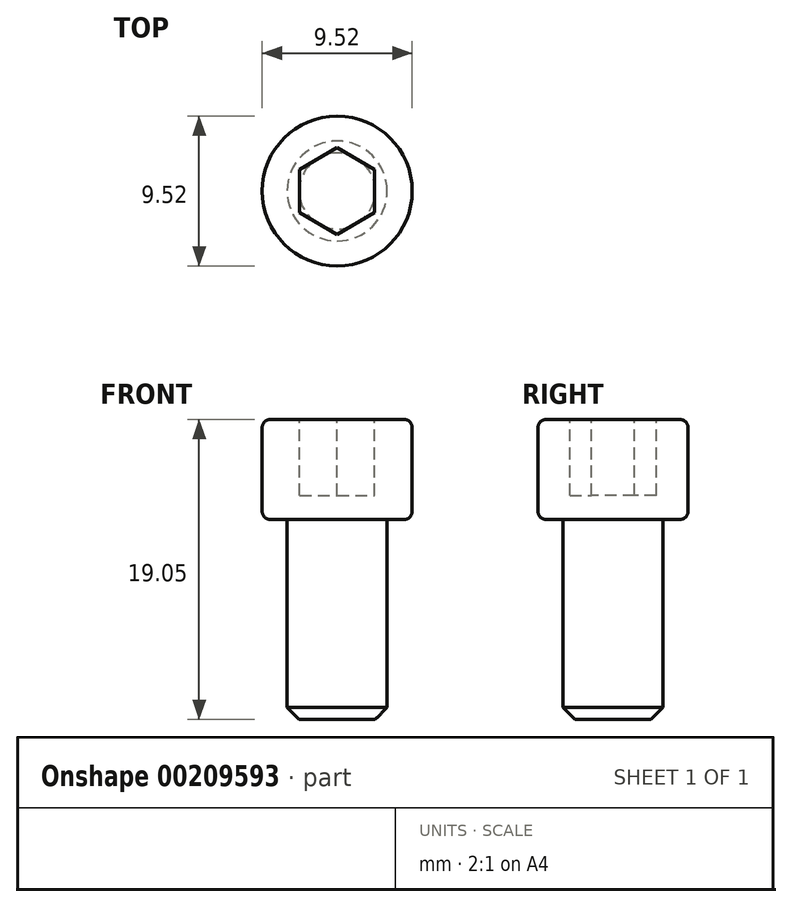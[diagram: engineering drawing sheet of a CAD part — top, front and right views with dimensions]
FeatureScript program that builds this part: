
annotation { "Feature Type Name" : "Feature", "Feature Type Description" : "" }
export const myFeature = defineFeature(function(context is Context, id is Id, definition is map)
    precondition{}
    {
        {
            var Q0;
            Q0=qCreatedBy(makeId("Top.planeOp"),FACE);
            var sketch = newSketch(context, id + "F0", { "sketchPlane" : qUnion([Q0])});
            skCircle(sketch, "E0", {"center": v(0, 0) * mm, "radius": 3.18 * mm});
            skSolve(sketch);
        }
        {
            var Q0;
            Q0=makeQuery(id+"F0.imprint","IMPRINT",FACE,{"disambiguationData":[TD([[makeQuery(id+"F0.imprint","IMPRINT",EDGE,{"derivedFrom":sQuery(id+"F0.wireOp",EDGE,"E0")}),1.0]])]});
            extrude(context, id + "F1", {"entities" : qUnion([Q0]), "oppositeDirection" : true, "depth" : 12.7 * mm});
        }
        {
            var Q0;
            Q0=qCreatedBy(makeId("Top.planeOp"),FACE);
            var sketch = newSketch(context, id + "F2", { "sketchPlane" : qUnion([Q0])});
            skCircle(sketch, "E1", {"center": v(0, 0) * mm, "radius": 4.76 * mm});
            skSolve(sketch);
        }
        {
            var Q0;
            Q0=makeQuery(id+"F2.imprint","IMPRINT",FACE,{"disambiguationData":[TD([[makeQuery(id+"F2.imprint","IMPRINT",EDGE,{"derivedFrom":sQuery(id+"F2.wireOp",EDGE,"E1")}),1.0]])]});
            extrude(context, id + "F3", {"entities" : qUnion([Q0]), "operationType" : NewBodyOperationType.ADD, "depth" : 6.35 * mm});
        }
        {
            var Q0;
            Q0=makeQuery(id+"F3.opExtrude","CAP_FACE",FACE,{"disambiguationData":[OSD([sQuery(id+"F2.wireOp",EDGE,"E1")])],"isStart":false});
            var sketch = newSketch(context, id + "F4", { "sketchPlane" : qUnion([Q0])});
            skCircle(sketch, "E2.cCircle", {"center": v(0, 0) * mm, "radius": 2.38 * mm, "construction": true});
            skLineSegment(sketch, "E2.0", {"start": v(2.38, 1.37) * mm, "end": v(2.38, -1.37) * mm});
            skLineSegment(sketch, "E2.1", {"start": v(2.38, -1.37) * mm, "end": v(0, -2.75) * mm});
            skLineSegment(sketch, "E2.2", {"start": v(0, -2.75) * mm, "end": v(-2.38, -1.37) * mm});
            skLineSegment(sketch, "E2.3", {"start": v(-2.38, -1.37) * mm, "end": v(-2.38, 1.37) * mm});
            skLineSegment(sketch, "E2.4", {"start": v(-2.38, 1.37) * mm, "end": v(0, 2.75) * mm});
            skLineSegment(sketch, "E2.5", {"start": v(0, 2.75) * mm, "end": v(2.38, 1.37) * mm});
            skPoint(sketch, "E2.0.midPoint", {"position": v(2.38, 0) * mm});
            skSolve(sketch);
        }
        {
            var Q0;
            Q0=makeQuery(id+"F4.imprint","IMPRINT",FACE,{"disambiguationData":[TD([[makeQuery(id+"F4.imprint","IMPRINT",EDGE,{"derivedFrom":sQuery(id+"F4.wireOp",EDGE,"E2.0")}),-1.0]])]});
            extrude(context, id + "F5", {"entities" : qUnion([Q0]), "operationType" : NewBodyOperationType.REMOVE, "oppositeDirection" : true, "depth" : 4.83 * mm});
        }
        {
            var Q0;
            Q0=makeQuery(id+"F1.opExtrude","CAP_EDGE",EDGE,{"disambiguationData":[OSD([sQuery(id+"F0.wireOp",EDGE,"E0")])],"isStart":false});
            chamfer(context, id + "F6", {"entities" : qUnion([Q0]), "chamferType" : ChamferType.OFFSET_ANGLE, "width" : 0.76 * mm, "oppositeDirection" : false, "angle" : 45 * degree, "tangentPropagation" : true});
        }
        {
            var Q0;
            Q0=qCreatedBy(makeId("Top.planeOp"),FACE);
            var Q1;
            Q1 = qBodyType(qCreatedBy(id + "F8" ,EDGE), BodyType.WIRE);
            cPlane(context, id + "F7", {"entities" : qUnion([Q0, Q1]), "cplaneType" : CPlaneType.OFFSET, "offset" : ((1 / 20) * 2) * mm, "oppositeDirection" : true, "width" : 152.4 * mm, "height" : 152.4 * mm});
        }
        {
            var Q0;
            Q0=qCreatedBy(id+"F7.planeOp",FACE);
            var sketch = newSketch(context, id + "F8", { "sketchPlane" : qUnion([Q0])});
            skCircle(sketch, "E3", {"center": v(0, 0) * mm, "radius": 2.38 * mm});
            skSolve(sketch);
        }
        {
            var Q0;
            Q0=sQuery(id+"F8.wireOp",EDGE,"E3");
            var Q1;
            Q1=makeQuery(id+"F6.opChamfer","BLEND_FACE",FACE,{"disambiguationData":[OSD([sQuery(id+"F0.wireOp",EDGE,"E0")])]});
            extrude(context, id + "F9", {"bodyType" : ToolBodyType.SURFACE, "surfaceEntities" : qUnion([Q0]), "endBound" : BoundingType.UP_TO_SURFACE, "oppositeDirection" : true, "endBoundEntityFace" : qUnion([Q1]), "depth" : 25.4 * mm});
        }
        {
            var Q0;
            Q0=makeQuery(id+"F3.opExtrude","CAP_EDGE",EDGE,{"disambiguationData":[OSD([sQuery(id+"F2.wireOp",EDGE,"E1")])],"isStart":false});
            var Q1;
            Q1=makeQuery(id+"F3.opExtrude","CAP_EDGE",EDGE,{"disambiguationData":[OSD([sQuery(id+"F2.wireOp",EDGE,"E1")])],"isStart":true});
            fillet(context, id + "F10", {"entities" : qUnion([Q0, Q1]), "radius" : 0.5 * mm, "tangentPropagation" : true, "allowEdgeOverflow" : false});
        }
    });
